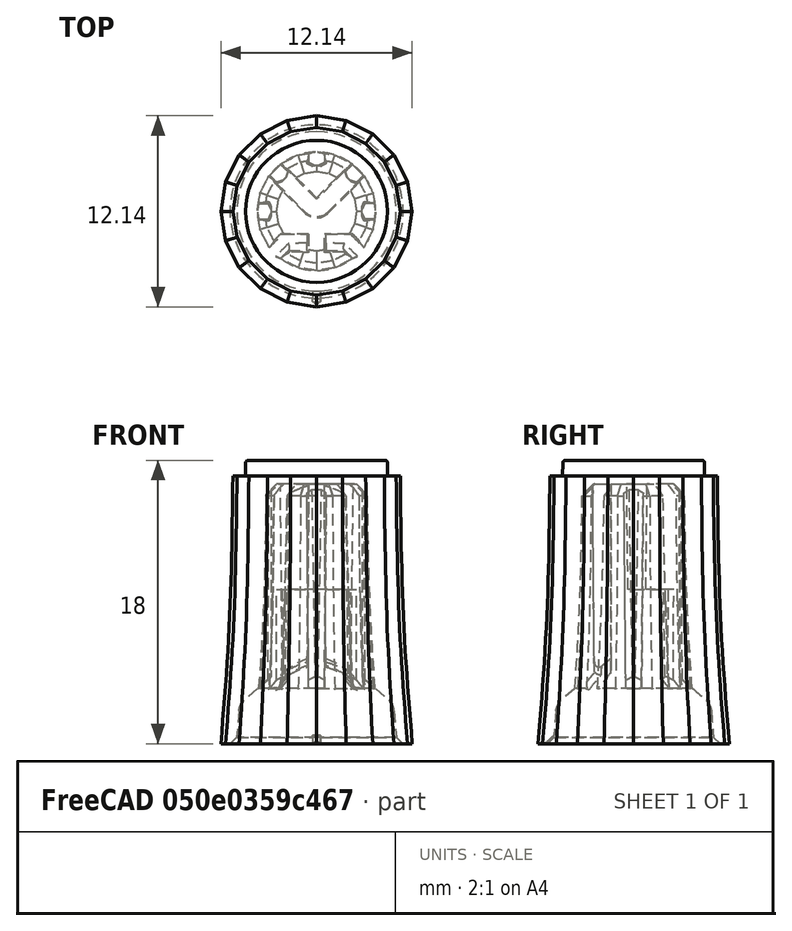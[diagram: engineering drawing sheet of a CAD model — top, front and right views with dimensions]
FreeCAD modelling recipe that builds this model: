
FCSTD DOCUMENT  (FreeCAD 1.0R39319 (Git))
Label: PLASTIC-KNOB-ENC_v2
License: All rights reserved
LicenseURL: https://en.wikipedia.org/wiki/All_rights_reserved
objects: TechDraw::DrawViewDimension×11, TechDraw::DrawHatch×10, Sketcher::SketchObject×5, TechDraw::DrawViewBalloon×5, TechDraw::DrawViewPart×5, TechDraw::DrawViewAnnotation×2, PartDesign::Pocket×2, PartDesign::Plane×2, PartDesign::PolarPattern×2, PartDesign::Pad×2, Part::Feature×1, PartDesign::Boolean×1, TechDraw::DrawSVGTemplate×1, PartDesign::Mirrored×1, PartDesign::CoordinateSystem×1, PartDesign::Body×1, TechDraw::DrawComplexSection×1, TechDraw::DrawPage×1
note: 56 computed .brp shape members not serialized (recipe doc carries the construction recipe); baked Part::Feature solids carry a one-line shape summary decoded from their .brp

FEATURE [Part::Feature] Part__Feature  label="potmeter"
  shape: bbox 15.71 x 15.32 x 34.99 mm, 134 faces (baked)
FEATURE [PartDesign::Boolean] Boolean
  Group = -> [Part__Feature]
  Suppressed = false
  Type = 0
  UsePlacement = false
FEATURE [TechDraw::DrawSVGTemplate] Template
  EditableTexts = COLOR=Black - RAL code: 9004; CreationDate=2025-07-31; E.G.APPROVED=APPROVED; FC-Scale=5:1; FC-Title=PLASTIC - KNOB - POT; IntechStudioLtd.=Intech Studio Ltd.; MATERIAL=ABS - Terluran GP22; REV=03; STANDARD=DIN 16742-TG4
  Height = 297
  Orientation = 1
  Template = <userpath>/Documents/grid-hardware/Manufacturing/FreeCAD_technical_drawing_template/A3_LandscapeTD_MODIFIED.svg
  Width = 420
FEATURE [Sketcher::SketchObject] Sketch
  ArcFitTolerance = 0
  AttachmentSupport = -> [XZ_Plane]
  FullyConstrained = true
  MakeInternals = false
  MapMode = 5
  Placement = pos=(0,0,0) rot=(1,0,0;1.5708rad)
  sketch-geometry (1):
    g0: LineSegment StartX=0 StartY=19 StartZ=0 EndX=0 EndY=-1 EndZ=0
  constraints (4):
    c: PointOnObject(g0,g-2)
    c: Vertical(g0)
    c: DistanceY(g0,g0) = 20
    c: DistanceY(g0,g-1) = 1
FEATURE [TechDraw::DrawViewDimension] Dimension010
  AngleOverride = false
  Arbitrary = false
  ArbitraryTolerances = false
  EqualTolerance = true
  ExtensionAngle = 0
  FormatSpec = %.2w
  FormatSpecOverTolerance = %+.2w
  FormatSpecUnderTolerance = %+.2w
  Inverted = false
  LineAngle = 0
  LockPosition = false
  MeasureType = 1
  OverTolerance = 0
  Rotation = 0
  ScaleType = 0
  TheoreticalExact = false
  Type = 2
  UnderTolerance = 0
  X = -41.9183
  Y = 15.656
FEATURE [TechDraw::DrawViewAnnotation] Annotation001
  Font = osifont
  LineSpace = 100
  LockPosition = false
  MaxWidth = -1
  Rotation = 0
  ScaleType = 0
  Text = AESTHETICAL SURFACES: | COLORED BLUE ON THE ISOMETRIC VIEWS: SPI - D2 | NO BURRS, NO PARTING LINES, | NO EJECTION MARKS | FREE OF ANY DEFECTS | FREE OF ANY WELD OR MELD LINES | NON VISIBLE GATE LOCATION ALLOWED | REMAINING BLACK SURFACES: SPI - B2
  TextSize = 3
  TextStyle = 0
  X = 264.167
  Y = 100.12
FEATURE [TechDraw::DrawViewDimension] Dimension012
  AngleOverride = false
  Arbitrary = false
  ArbitraryTolerances = false
  EqualTolerance = true
  ExtensionAngle = 0
  FormatSpec = (%.2w)
  FormatSpecOverTolerance = %+.2w
  FormatSpecUnderTolerance = %+.2w
  Inverted = false
  LineAngle = 0
  LockPosition = false
  MeasureType = 1
  OverTolerance = 0
  Rotation = 0
  ScaleType = 0
  TheoreticalExact = false
  Type = 2
  UnderTolerance = 0
  X = -37.4834
  Y = -5.49655
FEATURE [TechDraw::DrawViewBalloon] Balloon004
  BubbleShape = 2
  EndType = 6
  EndTypeScale = 1
  KinkLength = 0
  LockPosition = false
  OriginX = -50.6224
  OriginY = 14.8162
  Rotation = 0
  ScaleType = 0
  ShapeScale = 1
  SourceView = -> Dimension010
  Text = 2
  TextWrapLen = -1
  X = -51.7505
  Y = 12.4076
FEATURE [TechDraw::DrawViewAnnotation] Annotation002
  Font = osifont
  LineSpace = 100
  LockPosition = false
  MaxWidth = -1
  Rotation = 0
  ScaleType = 0
  Text = Section A-A
  TextSize = 4
  TextStyle = 0
  X = 193.568
  Y = 128.632
FEATURE [Sketcher::SketchObject] Sketch008
  ArcFitTolerance = 0
  AttachmentSupport = -> [XY_Plane]
  FullyConstrained = true
  MakeInternals = false
  MapMode = 5
  sketch-geometry (6):
    g0: ArcOfCircle CenterX=0 CenterY=0 CenterZ=0 NormalX=0 NormalY=0 NormalZ=1 AngleXU=0 Radius=2.95 StartAngle=0.615084 EndAngle=0.955712
    g1: LineSegment StartX=2.40934 StartY=1.70223 StartZ=0 EndX=2.05578 EndY=1.34868 EndZ=0
    g2: LineSegment StartX=2.05578 StartY=1.34868 StartZ=0 EndX=1.34868 EndY=2.05578 EndZ=0
    g3: LineSegment StartX=1.34868 StartY=2.05578 StartZ=0 EndX=1.70223 EndY=2.40934 EndZ=0
    g4: LineSegment [constr] StartX=2.08597 StartY=2.08597 StartZ=0 EndX=0 EndY=0 EndZ=0
    g5: GeomPoint [constr] X=1.70223 Y=1.70223 Z=0
  constraints (16):
    c: Coincident(g0,g-1)
    c: Diameter(g0) = 5.9
    c: Coincident(g2,g1)
    c: Coincident(g3,g2)
    c: PointOnObject(g4,g0)
    c: Coincident(g4,g0)
    c: Angle(g4,g-2) = 0.785398
    c: Parallel(g1,g4)
    c: Parallel(g4,g3)
    c: Perpendicular(g1,g2)
    c: Symmetric(g1,g2,g5)
    c: PointOnObject(g5,g4)
    c: Distance(g2) = 1
    c: Distance(g3) = 0.5
    c: Coincident(g0,g3)
    c: Coincident(g0,g1)
FEATURE [PartDesign::Pocket] Pocket
  BaseFeature = -> Boolean
  Direction = (0,0,-1)
  Length = 9.8
  Length2 = 5
  Profile = -> Sketch008
  ReferenceAxis = -> Sketch008 [N_Axis]
  Refine = true
  Reversed = true
  Suppressed = false
  Type = 0
FEATURE [PartDesign::Mirrored] Mirrored
  BaseFeature = -> Pocket
  MirrorPlane = -> Sketch008 [V_Axis]
  Originals = -> [Pocket]
  Refine = true
  Suppressed = false
  TransformMode = 0
FEATURE [Sketcher::SketchObject] Sketch009
  ArcFitTolerance = 0
  AttachmentSupport = -> [XY_Plane]
  FullyConstrained = true
  MakeInternals = false
  MapMode = 5
  sketch-geometry (5):
    g0: ArcOfCircle CenterX=0 CenterY=0 CenterZ=0 NormalX=0 NormalY=0 NormalZ=1 AngleXU=0 Radius=2.95 StartAngle=6.11287 EndAngle=6.4535
    g1: LineSegment StartX=2.90732 StartY=0.5 StartZ=0 EndX=2.40732 EndY=0.5 EndZ=0
    g2: LineSegment StartX=2.40732 StartY=0.5 StartZ=0 EndX=2.40732 EndY=-0.5 EndZ=0
    g3: LineSegment StartX=2.40732 StartY=-0.5 StartZ=0 EndX=2.90732 EndY=-0.5 EndZ=0
    g4: GeomPoint [constr] X=2.40732 Y=0 Z=0
  constraints (13):
    c: Coincident(g0,g-1)
    c: Diameter(g0) = 5.9
    c: Horizontal(g1)
    c: Coincident(g2,g1)
    c: Vertical(g2)
    c: Horizontal(g3)
    c: Coincident(g2,g3)
    c: Symmetric(g1,g2,g4)
    c: PointOnObject(g4,g-1)
    c: DistanceX(g1,g1) = 0.5
    c: DistanceY(g2,g2) = 1
    c: Coincident(g0,g1)
    c: Coincident(g0,g3)
FEATURE [PartDesign::Pocket] Pocket001
  BaseFeature = -> Mirrored
  Direction = (0,0,-1)
  Length = 16.5
  Length2 = 5
  Profile = -> Sketch009
  ReferenceAxis = -> Sketch009 [N_Axis]
  Refine = true
  Reversed = true
  Suppressed = false
  Type = 0
FEATURE [PartDesign::Plane] DatumPlane
  AttachmentOffset = pos=(0,0,0) rot=(0,-1,0;0.15708rad)
  AttachmentSupport = -> [XZ_Plane]
  Length = 67.9025
  MapMode = 5
  Placement = pos=(0,0,0) rot=(0.993863,-0.078219,-0.078219;1.57695rad)
  ResizeMode = 0
  Width = 60.6964
FEATURE [Sketcher::SketchObject] Sketch010
  ArcFitTolerance = 0
  AttachmentSupport = -> [DatumPlane]
  FullyConstrained = true
  MakeInternals = false
  MapMode = 5
  Placement = pos=(0,0,0) rot=(0.993863,-0.078219,-0.078219;1.57695rad)
  sketch-geometry (3):
    g0: LineSegment StartX=2.50536 StartY=16.5 StartZ=0 EndX=3.50536 EndY=15.4768 EndZ=0
    g1: LineSegment StartX=2.50536 StartY=16.5 StartZ=0 EndX=3.50536 EndY=16.5 EndZ=0
    g2: LineSegment StartX=3.50536 StartY=16.5 StartZ=0 EndX=3.50536 EndY=15.4768 EndZ=0
  constraints (9):
    c: DistanceY(g-1,g0) = 16.5
    c: DistanceX(g-1,g0) = 2.50536
    c: DistanceX(g0,g0) = 1
    c: Coincident(g1,g0)
    c: Coincident(g2,g1)
    c: Coincident(g2,g0)
    c: Horizontal(g1)
    c: Vertical(g2)
    c: Angle(g0,g1) = 0.796848
FEATURE [PartDesign::PolarPattern] PolarPattern
  Angle = 180
  Axis = -> Sketch009 [N_Axis]
  BaseFeature = -> Pocket001
  Mode = 0
  Occurrences = 3
  Offset = 120
  Originals = -> [Pocket001]
  Refine = true
  Suppressed = false
  TransformMode = 0
FEATURE [PartDesign::Pad] Pad001
  BaseFeature = -> PolarPattern
  Direction = (-0.156434,-0.987688,0)
  Length = 2
  Length2 = 10
  Midplane = true
  Profile = -> Sketch010
  ReferenceAxis = -> Sketch010 [N_Axis]
  Suppressed = false
  Type = 0
FEATURE [PartDesign::Plane] DatumPlane001
  AttachmentOffset = pos=(0,0,0) rot=(0,1,0;0.15708rad)
  AttachmentSupport = -> [XZ_Plane]
  Length = 67.9025
  MapMode = 5
  Placement = pos=(0,0,0) rot=(0.993863,0.078219,0.078219;1.57695rad)
  ResizeMode = 0
  Width = 60.6964
FEATURE [Sketcher::SketchObject] Sketch011
  ArcFitTolerance = 0
  AttachmentSupport = -> [DatumPlane001]
  FullyConstrained = true
  MakeInternals = false
  MapMode = 5
  Placement = pos=(0,0,0) rot=(0.993863,0.078219,0.078219;1.57695rad)
  sketch-geometry (3):
    g0: LineSegment StartX=2.50536 StartY=16.5 StartZ=0 EndX=3.50536 EndY=15.4768 EndZ=0
    g1: LineSegment StartX=3.50536 StartY=15.4768 StartZ=0 EndX=3.50536 EndY=16.5 EndZ=0
    g2: LineSegment StartX=3.50536 StartY=16.5 StartZ=0 EndX=2.50536 EndY=16.5 EndZ=0
  constraints (9):
    c: Coincident(g1,g0)
    c: Vertical(g1)
    c: Coincident(g2,g1)
    c: Coincident(g2,g0)
    c: Horizontal(g2)
    c: DistanceX(g0,g0) = 1
    c: DistanceY(g-1,g0) = 16.5
    c: DistanceX(g-1,g0) = 2.50536
    c: Angle(g0,g2) = 0.796848
FEATURE [PartDesign::Pad] Pad002
  BaseFeature = -> Pad001
  Direction = (0.156434,-0.987688,0)
  Length = 2
  Length2 = 10
  Midplane = true
  Profile = -> Sketch011
  ReferenceAxis = -> Sketch011 [N_Axis]
  Suppressed = false
  Type = 0
FEATURE [PartDesign::PolarPattern] PolarPattern001
  Angle = 180
  Axis = -> Z_Axis
  BaseFeature = -> Pad002
  Mode = 0
  Occurrences = 3
  Offset = 120
  Originals = -> [Pad001,Pad002]
  Suppressed = false
  TransformMode = 0
FEATURE [PartDesign::CoordinateSystem] LCS_1
  AttacherType = Attacher::AttachEngine3D
  AttachmentSupport = -> [PolarPattern001]
  MapMode = 5
  Placement = pos=(0,0,9.8) rot=(1,0,0;3.14159rad)
FEATURE [PartDesign::Body] Body  label="PLASTIC-KNOB-ENC_v2"
  AllowCompound = false
  Group = -> [Boolean,Sketch,Sketch008,Pocket,Mirrored,Sketch009,Pocket001,DatumPlane,Sketch010,PolarPattern,Pad001,DatumPlane001,Sketch011,Pad002,PolarPattern001,LCS_1]
  Origin = -> Origin
  Tip = -> PolarPattern001
FEATURE [TechDraw::DrawViewPart] View
  CoarseView = false
  Direction = (0,-1,0)
  Focus = 100
  HardHidden = false
  IsoCount = 0
  IsoHidden = false
  IsoVisible = true
  LockPosition = false
  Perspective = false
  Rotation = 0
  Scale = 5
  ScaleType = 2
  ScrubCount = 0
  SeamHidden = false
  SeamVisible = true
  SmoothHidden = false
  SmoothVisible = true
  Source = -> [Body]
  X = 98.421
  XDirection = (1,0,-1e-06)
  Y = 192.804
FEATURE [TechDraw::DrawComplexSection] ComplexSection  label="Section A - A"
  BaseView = -> View
  CoarseView = false
  CutSurfaceDisplay = 2
  CuttingToolWireObject = -> Sketch
  Direction = (-1,0,1e-06)
  FileGeomPattern = C:/Program Files/FreeCAD 0.21/data/Mod/TechDraw/PAT/FCPAT.pat
  FileHatchPattern = C:/Program Files/FreeCAD 0.21/data/Mod/TechDraw/Patterns/simple.svg
  Focus = 100
  FuseBeforeCut = false
  HardHidden = false
  HatchOffset = (0,0,0)
  HatchRotation = 0
  HatchScale = 1
  IsoCount = 0
  IsoHidden = false
  IsoVisible = false
  LockPosition = false
  NameGeomPattern = Gyémánt bevonatú
  Perspective = false
  ProjectionStrategy = 0
  Rotation = -90
  Scale = 5
  ScaleType = 2
  ScrubCount = 0
  SeamHidden = false
  SeamVisible = true
  SectionDirection = 4
  SectionLineStretch = 1
  SectionNormal = (-1,0,1e-06)
  SectionOrigin = (0,0,0)
  SectionSymbol = A
  SmoothHidden = false
  SmoothVisible = true
  Source = -> [Body]
  TrimAfterCut = false
  UsePreviousCut = false
  X = 193.568
  XDirection = (-1e-06,0,-1)
  Y = 192.821
FEATURE [TechDraw::DrawViewPart] View003
  CoarseView = false
  Direction = (-0.57735,-0.57735,0.57735)
  Focus = 100
  HardHidden = false
  IsoCount = 0
  IsoHidden = false
  IsoVisible = true
  LockPosition = false
  Perspective = false
  Rotation = 0
  Scale = 2
  ScaleType = 2
  ScrubCount = 0
  SeamHidden = false
  SeamVisible = true
  SmoothHidden = false
  SmoothVisible = true
  Source = -> [Body]
  X = 379.046
  XDirection = (0.707107,-0.707107,0)
  Y = 107.401
FEATURE [TechDraw::DrawViewPart] View004
  CoarseView = false
  Direction = (-0.57735,-0.57735,-0.57735)
  Focus = 100
  HardHidden = false
  IsoCount = 0
  IsoHidden = false
  IsoVisible = true
  LockPosition = false
  Perspective = false
  Rotation = 0
  Scale = 2
  ScaleType = 2
  ScrubCount = 0
  SeamHidden = false
  SeamVisible = true
  SmoothHidden = false
  SmoothVisible = true
  Source = -> [Body]
  X = 337.082
  XDirection = (0.707106,-0.707106,0)
  Y = 107.401
FEATURE [TechDraw::DrawHatch] Hatch001  label="Hatch001F2"
  HatchPattern = C:/Program Files/FreeCAD 0.21/data/Mod/TechDraw/Patterns/solid.svg
  Source = -> View003 [Face2,Face13,Face4,Face5,Face3,Face6,Face9,Face8,Face7,Face12,Face11,Face10]
FEATURE [TechDraw::DrawHatch] Hatch002  label="Hatch002F1"
  HatchPattern = C:/Program Files/FreeCAD 0.21/data/Mod/TechDraw/Patterns/solid.svg
  Source = -> View003 [Face1]
FEATURE [TechDraw::DrawViewBalloon] Balloon
  BubbleShape = 1
  EndType = 3
  EndTypeScale = 1
  KinkLength = 0
  LockPosition = false
  OriginX = -2.29422
  OriginY = 3.04373
  Rotation = 0
  ScaleType = 0
  ShapeScale = 1
  SourceView = -> View004
  TextWrapLen = -1
  X = -16.2526
  Y = -5.35905
FEATURE [TechDraw::DrawViewPart] View002
  CoarseView = false
  Direction = (1e-06,0,1)
  Focus = 100
  HardHidden = false
  IsoCount = 0
  IsoHidden = false
  IsoVisible = true
  LockPosition = false
  Perspective = false
  Rotation = 0
  Scale = 5
  ScaleType = 2
  ScrubCount = 0
  SeamHidden = false
  SeamVisible = true
  SmoothHidden = false
  SmoothVisible = true
  Source = -> [Body]
  X = 100.462
  XDirection = (1,0,-1e-06)
  Y = 74.8021
FEATURE [TechDraw::DrawViewDimension] Dimension009
  AngleOverride = false
  Arbitrary = false
  ArbitraryTolerances = false
  EqualTolerance = true
  ExtensionAngle = 0
  FormatSpec = 10× %.2w
  FormatSpecOverTolerance = %+.2w
  FormatSpecUnderTolerance = %+.2w
  Inverted = false
  LineAngle = 0
  LockPosition = false
  MeasureType = 1
  OverTolerance = 0
  References2D = -> [View002]
  Rotation = 0
  ScaleType = 0
  TheoreticalExact = false
  Type = 0
  UnderTolerance = 0
  X = -39.2324
  Y = 9.93901
FEATURE [TechDraw::DrawViewDimension] Dimension013
  AngleOverride = false
  Arbitrary = false
  ArbitraryTolerances = false
  EqualTolerance = true
  ExtensionAngle = 0
  FormatSpec = ⌀%.2w
  FormatSpecOverTolerance = %+.2w
  FormatSpecUnderTolerance = %+.2w
  Inverted = false
  LineAngle = 0
  LockPosition = false
  MeasureType = 1
  OverTolerance = 0
  References2D = -> [View]
  Rotation = 0
  ScaleType = 0
  TheoreticalExact = false
  Type = 1
  UnderTolerance = 0
  X = -8.9e-05
  Y = 66.4443
FEATURE [TechDraw::DrawViewDimension] Dimension014
  AngleOverride = false
  Arbitrary = false
  ArbitraryTolerances = false
  EqualTolerance = true
  ExtensionAngle = 0
  FormatSpec = %.2w
  FormatSpecOverTolerance = %+.2w
  FormatSpecUnderTolerance = %+.2w
  Inverted = false
  LineAngle = 0
  LockPosition = false
  MeasureType = 1
  OverTolerance = 0
  References2D = -> [View]
  Rotation = 0
  ScaleType = 0
  TheoreticalExact = false
  Type = 2
  UnderTolerance = 0
  X = 38.805
  Y = 45.2486
FEATURE [TechDraw::DrawViewDimension] Dimension015
  AngleOverride = false
  Arbitrary = false
  ArbitraryTolerances = false
  EqualTolerance = true
  ExtensionAngle = 0
  FormatSpec = %.2w
  FormatSpecOverTolerance = %+.2w
  FormatSpecUnderTolerance = %+.2w
  Inverted = false
  LineAngle = 0
  LockPosition = false
  MeasureType = 1
  OverTolerance = 0
  References2D = -> [View]
  Rotation = 0
  ScaleType = 0
  TheoreticalExact = false
  Type = 2
  UnderTolerance = 0
  X = -48.6863
  Y = 2.49998
FEATURE [TechDraw::DrawViewPart] View001
  CoarseView = false
  Direction = (-1e-06,0,-1)
  Focus = 100
  HardHidden = false
  IsoCount = 0
  IsoHidden = false
  IsoVisible = true
  LockPosition = false
  Perspective = false
  Rotation = 0
  Scale = 5
  ScaleType = 2
  ScrubCount = 0
  SeamHidden = false
  SeamVisible = true
  SmoothHidden = false
  SmoothVisible = true
  Source = -> [Body]
  X = 305.681
  XDirection = (1,0,-1e-06)
  Y = 190.563
FEATURE [TechDraw::DrawViewDimension] Dimension017
  AngleOverride = false
  Arbitrary = false
  ArbitraryTolerances = false
  BoxCorners = (2) [(-30.374,-30.374,-1e-07),(30.374,30.374,1e-07)]
  EqualTolerance = true
  ExtensionAngle = 0
  FormatSpec = ⌀%.2w
  FormatSpecOverTolerance = %+.2w
  FormatSpecUnderTolerance = %+.2w
  Inverted = false
  LineAngle = 0
  LockPosition = false
  MeasureType = 1
  OverTolerance = 0
  References2D = -> [View001]
  Rotation = 0
  ScaleType = 0
  TheoreticalExact = false
  Type = 5
  UnderTolerance = 0
  X = -43.4
  Y = 27.6231
FEATURE [TechDraw::DrawViewDimension] Dimension
  AngleOverride = false
  Arbitrary = false
  ArbitraryTolerances = false
  BoxCorners = (2) [(-30.374,-45,-1e-07),(30.374,45,1e-07)]
  EqualTolerance = true
  ExtensionAngle = 0
  FormatSpec = %.2w
  FormatSpecOverTolerance = %+.2w
  FormatSpecUnderTolerance = %+.2w
  Inverted = false
  LineAngle = 0
  LockPosition = false
  MeasureType = 1
  OverTolerance = 0.1
  References2D = -> [ComplexSection]
  Rotation = 0
  ScaleType = 0
  TheoreticalExact = false
  Type = 2
  UnderTolerance = -0.1
  X = 31.0773
  Y = -20.5
FEATURE [TechDraw::DrawViewDimension] Dimension021
  AngleOverride = false
  Arbitrary = false
  ArbitraryTolerances = false
  BoxCorners = (2) [(-30.374,-45,-1e-07),(30.374,45,1e-07)]
  EqualTolerance = false
  ExtensionAngle = 0
  FormatSpec = ⌀%.2w
  FormatSpecOverTolerance = %+.2w
  FormatSpecUnderTolerance = %+.2w
  Inverted = false
  LineAngle = 0
  LockPosition = false
  MeasureType = 1
  OverTolerance = 0.1
  References2D = -> [ComplexSection]
  Rotation = 0
  ScaleType = 0
  TheoreticalExact = false
  Type = 1
  UnderTolerance = 0
  X = -0.045274
  Y = -42.8297
FEATURE [TechDraw::DrawViewDimension] Dimension022
  AngleOverride = false
  Arbitrary = false
  ArbitraryTolerances = false
  BoxCorners = (2) [(-30.374,-30.374,-1e-07),(30.374,30.374,1e-07)]
  EqualTolerance = true
  ExtensionAngle = 0
  FormatSpec = %.2w
  FormatSpecOverTolerance = %+.2w
  FormatSpecUnderTolerance = %+.2w
  Inverted = false
  LineAngle = 0
  LockPosition = false
  MeasureType = 1
  OverTolerance = 0.05
  References2D = -> [View001]
  Rotation = 0
  ScaleType = 0
  TheoreticalExact = false
  Type = 1
  UnderTolerance = -0.05
  X = -5.1e-05
  Y = 54.1432
FEATURE [TechDraw::DrawViewDimension] Dimension023
  AngleOverride = false
  Arbitrary = false
  ArbitraryTolerances = false
  BoxCorners = (2) [(-30.374,-30.374,-1e-07),(30.374,30.374,1e-07)]
  EqualTolerance = true
  ExtensionAngle = 0
  FormatSpec = %.2w
  FormatSpecOverTolerance = %+.2w
  FormatSpecUnderTolerance = %+.2w
  Inverted = false
  LineAngle = 0
  LockPosition = false
  MeasureType = 1
  OverTolerance = 0.05
  References2D = -> [View001]
  Rotation = 0
  ScaleType = 0
  TheoreticalExact = false
  Type = 2
  UnderTolerance = -0.05
  X = 37.6716
  Y = 24.7624
FEATURE [TechDraw::DrawViewBalloon] Balloon009
  BubbleShape = 2
  EndType = 0
  EndTypeScale = 1
  KinkLength = 5
  LockPosition = false
  OriginX = -5.92613
  OriginY = 0.938607
  Rotation = 0
  ScaleType = 0
  ShapeScale = 1
  SourceView = -> View001
  Text = 3
  TextWrapLen = -1
  X = -11.2478
  Y = 3.14051
FEATURE [TechDraw::DrawViewBalloon] Balloon010
  BubbleShape = 2
  EndType = 0
  EndTypeScale = 1
  KinkLength = 5
  LockPosition = false
  OriginX = -1.98815
  OriginY = 12.4234
  Rotation = 0
  ScaleType = 0
  ShapeScale = 1
  SourceView = -> View001
  Text = 3
  TextWrapLen = -1
  X = -5.51177
  Y = 10.7925
FEATURE [TechDraw::DrawViewBalloon] Balloon011
  BubbleShape = 2
  EndType = 0
  EndTypeScale = 1
  KinkLength = 5
  LockPosition = false
  OriginX = 11.1664
  OriginY = -5.13173
  Rotation = 0
  ScaleType = 0
  ShapeScale = 1
  SourceView = -> View001
  Text = 3
  TextWrapLen = -1
  X = 11.5702
  Y = 3.12692
FEATURE [TechDraw::DrawPage] Page  label="PLASTIC-KNOB-ENC_Drawing"
  KeepUpdated = true
  NextBalloonIndex = 11
  ProjectionType = 0
  Template = -> Template
  Views = -> [View,View001,View002,ComplexSection,Dimension009,View003,View004,Annotation001,Balloon,Annotation002,Dimension013,Dimension014,Dimension015,Dimension017,Dimension,Dimension021,Dimension022,Dimension023,Balloon009,Balloon010,Balloon011]
FEATURE [TechDraw::DrawHatch] Hatch012
  HatchPattern = /app/share/Mod/TechDraw/Patterns/solid.svg
  Source = -> View004 [Face12,Face7,Face4,Face3,Face5,Face6,Face9]
FEATURE [TechDraw::DrawHatch] Hatch013
  HatchPattern = /app/share/Mod/TechDraw/Patterns/solid.svg
  Source = -> View004 [Face1,Face2,Face15,Face18,Face16,Face19]
FEATURE [TechDraw::DrawHatch] Hatch014
  HatchPattern = /app/share/Mod/TechDraw/Patterns/solid.svg
  Source = -> View004 [Face20,Face21,Face29,Face26,Face24,Face22,Face23,Face27,Face28]
FEATURE [TechDraw::DrawHatch] Hatch015
  HatchPattern = /app/share/Mod/TechDraw/Patterns/solid.svg
  Source = -> View004 [Face11,Face8,Face17]
FEATURE [TechDraw::DrawHatch] Hatch016
  HatchPattern = /app/share/Mod/TechDraw/Patterns/solid.svg
  Source = -> View004 [Face14]
FEATURE [TechDraw::DrawHatch] Hatch017
  HatchPattern = /app/share/Mod/TechDraw/Patterns/solid.svg
  Source = -> View004 [Face10]
FEATURE [TechDraw::DrawHatch] Hatch018
  HatchPattern = /app/share/Mod/TechDraw/Patterns/solid.svg
  Source = -> View004 [Face13]
FEATURE [TechDraw::DrawHatch] Hatch019
  HatchPattern = /app/share/Mod/TechDraw/Patterns/solid.svg
  Source = -> View004 [Face25,Face30]
